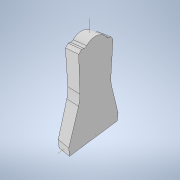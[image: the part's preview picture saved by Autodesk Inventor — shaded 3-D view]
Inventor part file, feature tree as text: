
AUTODESK INVENTOR PART (.ipt)
format: ipt  version: 2021.1 (Build 251245000, 245)  size: 135,680 bytes
history: native  units: in
note: dims shown in document units (in); Inventor stores cm internally (conversion verified against a paired STEP export)
features: extrude x1, sketch x1
ambient origin geometry x8: Origin, YZ Plane, XZ Plane, XY Plane, X Axis, Y Axis, Z Axis, Center Point
bodies: Solid1 (feature_tree)
feature tree (2):
  extrude  "Extrusion1"  Depth=2.0in
  sketch  "Sketch1"  dims[d0=9.2in d1=1.5in d2=1.5in d3=6.5in d4=6.5in d5=13.7in d6=0.125in d7=5.0in d8=4.0in d9=12.5in d10=0.5in d11=0.5in d12=0.4in d13=45.0deg d14=0.4in d15=45.0deg d16=2.0in d17=0.0in]
